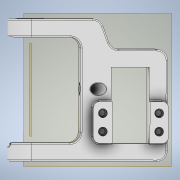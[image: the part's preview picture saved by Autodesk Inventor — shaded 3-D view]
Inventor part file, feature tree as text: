
AUTODESK INVENTOR PART (.ipt)
format: ipt  version: 2020.3 (Build 243373000, 373)  size: 545,280 bytes
history: native  units: mm
features: fillet x11, sketch x8, extrude x6, hole x5, plane x4, chamfer x1
ambient origin geometry x8: Origin, YZ Plane, XZ Plane, XY Plane, X Axis, Y Axis, Z Axis, Center Point
bodies: Solid1 (feature_tree)
feature tree (35):
  sketch  "Sketch1"  dims[d4=24.6mm d5=12.4mm]
  extrude  "Extrusion1"  Depth=12.4mm
  hole  "Hole1"  [1 undecoded]
  fillet  "Fillet1"  Radius=23.5mm
  fillet  "Fillet2"  Radius=34.5mm
  sketch  "Sketch2"  dims[d9=6.0mm d11=10.0mm d12=23.5mm d14=34.5mm]
  hole  "Hole2"  [1 undecoded]
  sketch  "Sketch8"  dims[d19=1.9mm d20=6.0mm d21=4.0mm d22=2.0mm d23=90.0deg d24=10.0mm d25=20.594885mm]
  extrude  "Extrusion3"  Depth=6.0mm
  extrude  "Extrusion4"  Depth=3.7mm
  hole  "Hole5"  [1 undecoded]
  fillet  "Fillet4"  Radius=10.0mm
  fillet  "Fillet9"  Radius=3.5mm
  fillet  "Fillet10"  Radius=0.5mm
  fillet  "Fillet5"  Radius=0.5mm
  fillet  "Fillet6"  Radius=28.4mm
  hole  "Hole4"  [1 undecoded]
  fillet  "Fillet11"  Radius=6.0mm
  extrude  "Extrusion6"  Depth=2.0mm
  plane  "Work Plane1"
  extrude  "Extrusion7"  Depth=0.5mm
  fillet  "Fillet12"  Radius=2.0mm
  hole  "Hole6"  [1 undecoded]
  plane  "Work Plane3"
  extrude  "Extrusion8"  Depth=2.0mm
  chamfer  "Chamfer1"  Distance=0.3mm
  fillet  "Fillet13"  Radius=0.2mm
  fillet  "Fillet14"  [1 undecoded]
  plane  "Work Plane5"
  plane  "Work Plane6"
  sketch  "Sketch3"  dims[d16=6.0mm d17=15.0mm d18=0.0mm]
  sketch  "Sketch9"  dims[d27=8.8mm d28=6.0mm d29=4.0mm d30=2.0mm d31=90.0deg d32=8.0mm d33=20.594885mm d34=6.0mm]
  sketch  "Sketch10"  dims[d37=7.2mm d38=3.7mm]
  sketch  "Sketch11"  dims[d39=12.1mm d40=3.5mm d41=0.0mm d42=10.0mm d43=0.0mm d53=3.5mm d54=0.5mm d55=0.5mm d57=28.4mm]
  sketch  "Sketch12"  dims[d58=6.8mm d59=20.92mm d60=0.0mm d61=6.0mm d62=3.0mm d63=6.0mm d64=4.0mm d65=2.0mm d66=90.0deg d67=4.3mm d68=0.0mm d70=2.0mm d71=0.5mm d72=2.0mm d74=2.0mm d75=2.0mm d76=1.0mm d77=6.0mm d78=4.0mm d79=2.0mm d80=90.0deg d81=8.0mm d82=20.594885mm d83=0.3mm d84=0.2mm d85=0.0mm d86=0.0mm d87=1.0mm d88=3.5mm d89=-9.075712mm d90=4.0mm d91=4.0mm d92=1.0mm d93=33.941mm d94=0.0mm d95=0.2mm d96=2.1mm d97=6.0mm d98=4.0mm d99=2.0mm d100=90.0deg d101=7.3mm d102=0.0mm d103=24.0mm d104=7.0mm d105=7.0mm d106=0.0mm d107=0.2mm d108=0.8mm d109=45.0deg d110=1.0mm d111=2.0mm d112=3.490659mm d113=16.0mm d114=-7.5mm]
note: 6 required parameter values undecoded (feature->parameter linkage not recoverable at this tier; creation-order binding heuristic only, values carry confidence <= 0.55)
